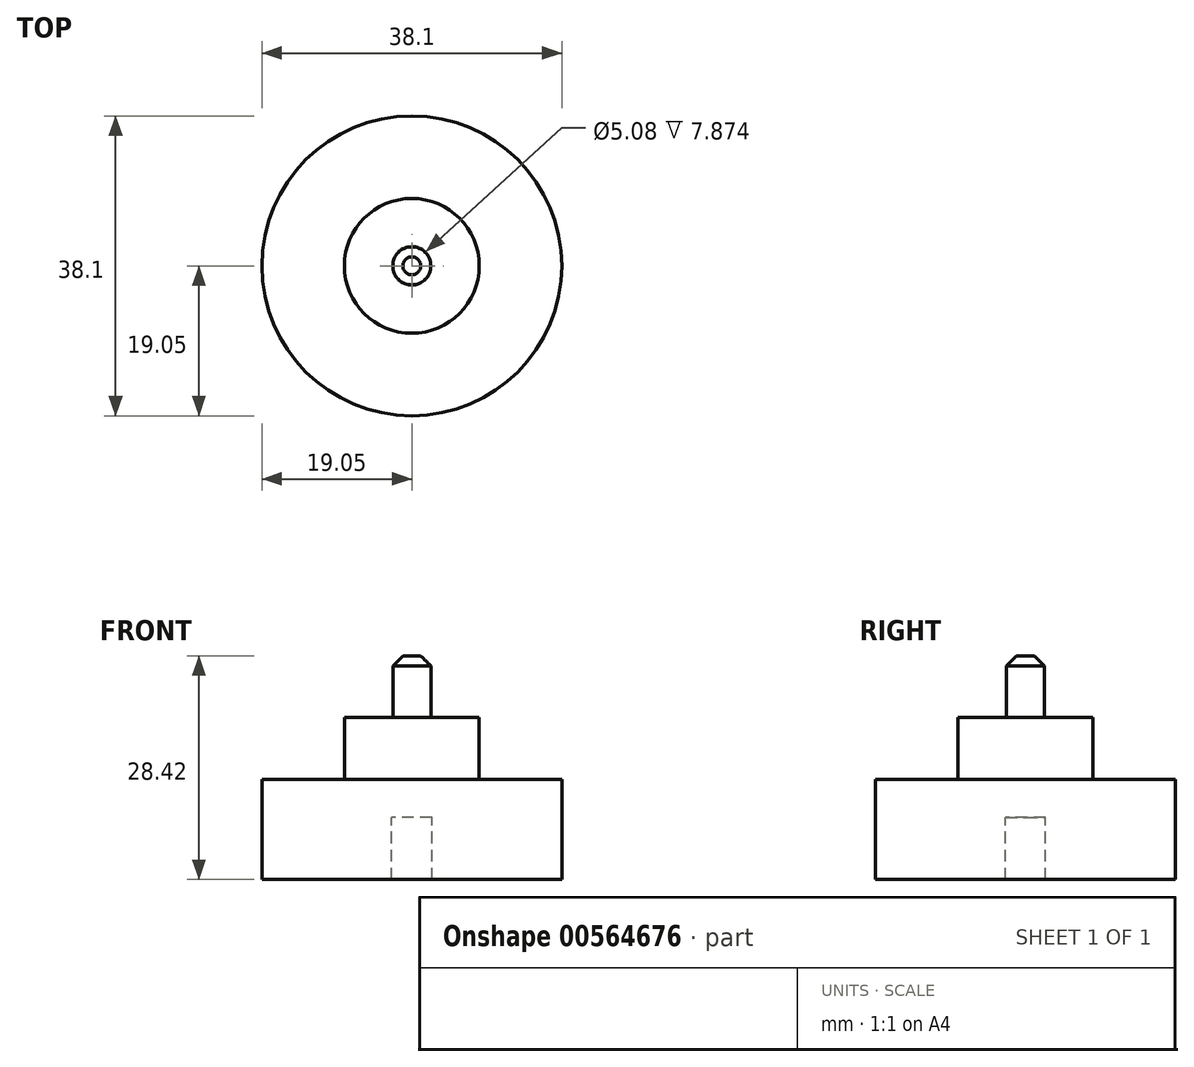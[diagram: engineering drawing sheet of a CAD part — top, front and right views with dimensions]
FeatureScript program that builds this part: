
annotation { "Feature Type Name" : "Feature", "Feature Type Description" : "" }
export const myFeature = defineFeature(function(context is Context, id is Id, definition is map)
    precondition{}
    {
        {
            var Q0;
            Q0=qCreatedBy(makeId("Front.planeOp"),FACE);
            var sketch = newSketch(context, id + "F0", { "sketchPlane" : qUnion([Q0])});
            skLineSegment(sketch, "E0", {"start": v(19.05, 0) * mm, "end": v(19.05, 12.7) * mm});
            skLineSegment(sketch, "E1", {"start": v(19.05, 12.7) * mm, "end": v(8.56, 12.7) * mm});
            skLineSegment(sketch, "E2", {"start": v(2.41, 20.57) * mm, "end": v(8.56, 20.57) * mm});
            skLineSegment(sketch, "E3", {"start": v(8.56, 20.57) * mm, "end": v(8.56, 12.7) * mm});
            skPoint(sketch, "E3.endSnap0", {"position": v(9.53, 12.7) * mm});
            skLineSegment(sketch, "E4", {"start": v(0, 28.42) * mm, "end": v(2.41, 28.42) * mm});
            skLineSegment(sketch, "E5", {"start": v(2.41, 28.42) * mm, "end": v(2.41, 20.57) * mm});
            skPoint(sketch, "E5.endSnap0", {"position": v(4.28, 20.57) * mm});
            skPoint(sketch, "E6.end.orphan", {"position": v(0, 20.57) * mm});
            skPoint(sketch, "E6.start.orphan", {"position": v(0, 12.7) * mm});
            skLineSegment(sketch, "E7", {"start": v(2.54, 0) * mm, "end": v(2.54, 7.87) * mm});
            skLineSegment(sketch, "E8", {"start": v(2.54, 7.87) * mm, "end": v(0, 7.87) * mm});
            skLineSegment(sketch, "E9", {"start": v(2.54, 0) * mm, "end": v(19.05, 0) * mm});
            skLineSegment(sketch, "E10", {"start": v(0, 28.42) * mm, "end": v(0, 7.87) * mm});
            skSolve(sketch);
        }
        {
            var Q0;
            Q0 = qSketchRegion(id + "F0", true);
            var Q1;
            Q1=sQuery(id+"F0.wireOp",EDGE,"E10");
            revolve(context, id + "F1", {"entities" : qUnion([Q0]), "axis" : qUnion([Q1]), "revolveType" : RevolveType.FULL});
        }
        {
            var Q0;
            Q0=makeQuery(id+"F1.opRevolve","SWEPT_EDGE",EDGE,{"disambiguationData":[OSD([sQuery(id+"F0.wireOp",EDGE,"E4"),sQuery(id+"F0.wireOp",EDGE,"E5")])]});
            chamfer(context, id + "F2", {"entities" : qUnion([Q0]), "width" : 1.27 * mm, "tangentPropagation" : true});
        }
    });
